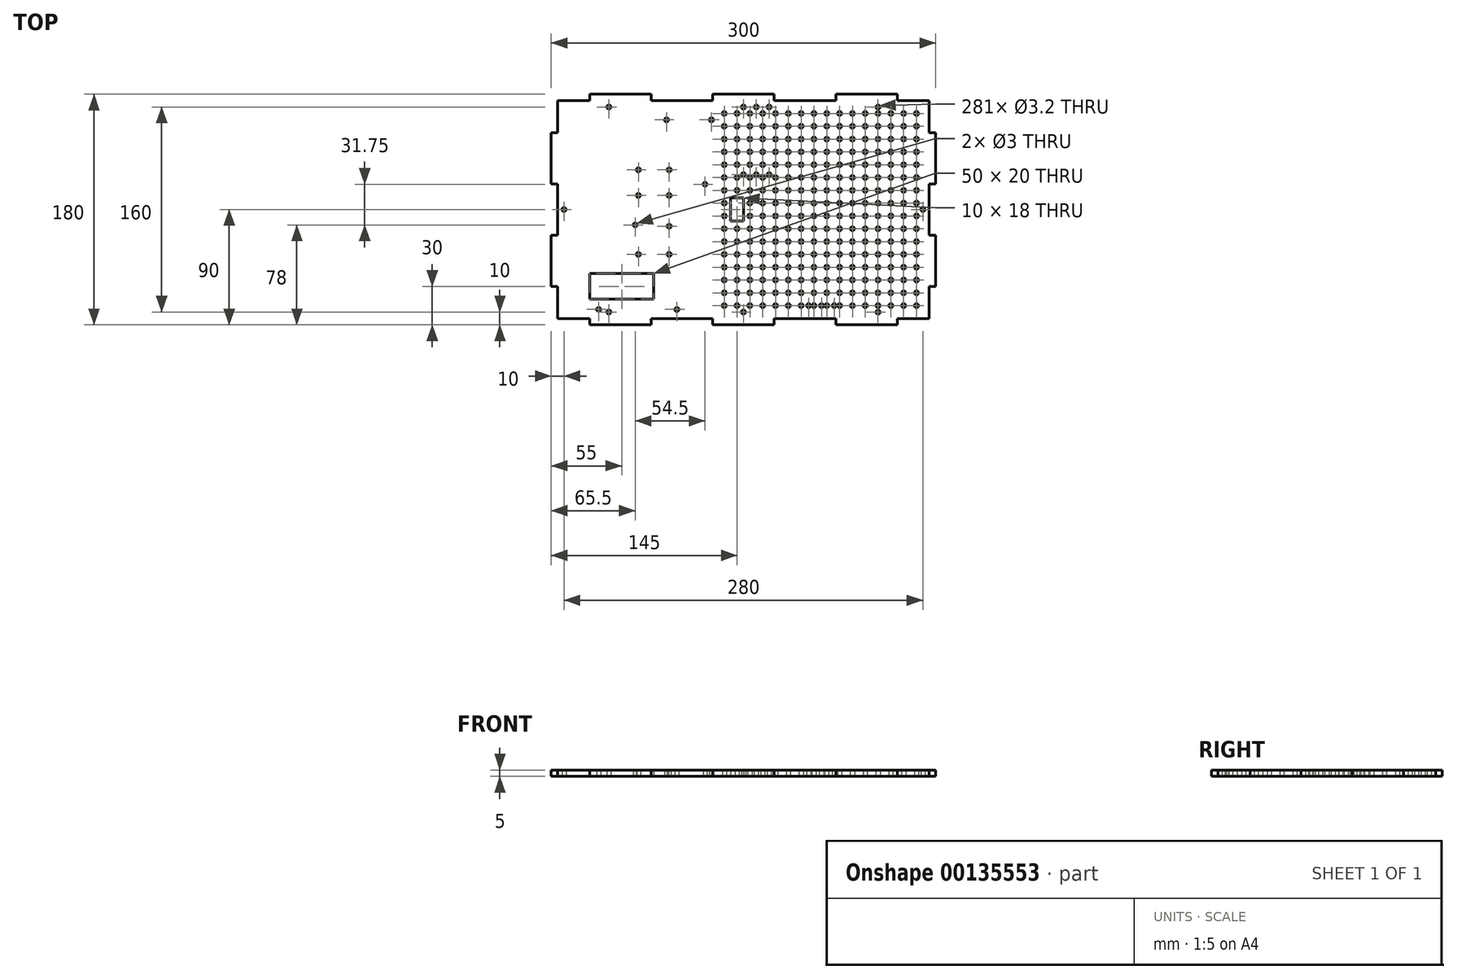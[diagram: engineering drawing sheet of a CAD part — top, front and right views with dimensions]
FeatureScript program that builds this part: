
annotation { "Feature Type Name" : "Feature", "Feature Type Description" : "" }
export const myFeature = defineFeature(function(context is Context, id is Id, definition is map)
    precondition{}
    {
        {
            var Q0;
            Q0=qCreatedBy(makeId("Top.planeOp"),FACE);
            var sketch = newSketch(context, id + "F0", { "sketchPlane" : qUnion([Q0])});
            skLineSegment(sketch, "E0", {"start": v(-150, 0) * mm, "end": v(150, 0) * mm, "construction": true});
            skLineSegment(sketch, "E1", {"start": v(0, 90) * mm, "end": v(0, -90) * mm, "construction": true});
            skLineSegment(sketch, "E2.bottom", {"start": v(-120, 90) * mm, "end": v(-72, 90) * mm});
            skLineSegment(sketch, "E2.top", {"start": v(-120, -90) * mm, "end": v(-72, -90) * mm});
            skLineSegment(sketch, "E2.left", {"start": v(-150, 60) * mm, "end": v(-150, -60) * mm});
            skLineSegment(sketch, "E2.right", {"start": v(150, 60) * mm, "end": v(150, -60) * mm});
            skLineSegment(sketch, "E3.bottom", {"start": v(-120, 85) * mm, "end": v(120, 85) * mm, "construction": true});
            skLineSegment(sketch, "E3.top", {"start": v(-145, -85) * mm, "end": v(145, -85) * mm, "construction": true});
            skLineSegment(sketch, "E3.left", {"start": v(-145, -60) * mm, "end": v(-145, -85) * mm, "construction": true});
            skLineSegment(sketch, "E3.right", {"start": v(145, -60) * mm, "end": v(145, -85) * mm, "construction": true});
            skLineSegment(sketch, "E4", {"start": v(-145, 85) * mm, "end": v(-120, 85) * mm});
            skLineSegment(sketch, "E5", {"start": v(-145, 85) * mm, "end": v(-145, 60) * mm});
            skLineSegment(sketch, "E6", {"start": v(-120, 85) * mm, "end": v(-120, 90) * mm});
            skLineSegment(sketch, "E7", {"start": v(-145, 60) * mm, "end": v(-150, 60) * mm});
            skLineSegment(sketch, "E8.MirrorCS", {"start": v(-120, -85) * mm, "end": v(-120, -90) * mm});
            skLineSegment(sketch, "E9.MirrorCS", {"start": v(-145, -85) * mm, "end": v(-120, -85) * mm});
            skLineSegment(sketch, "E10.MirrorCS", {"start": v(-145, -60) * mm, "end": v(-150, -60) * mm});
            skLineSegment(sketch, "E11.MirrorCS", {"start": v(-145, -85) * mm, "end": v(-145, -60) * mm});
            skLineSegment(sketch, "E12.MirrorCS", {"start": v(145, 60) * mm, "end": v(150, 60) * mm});
            skLineSegment(sketch, "E13.MirrorCS", {"start": v(145, 85) * mm, "end": v(145, 60) * mm});
            skLineSegment(sketch, "E14.MirrorCS", {"start": v(145, 85) * mm, "end": v(120, 85) * mm});
            skLineSegment(sketch, "E15.MirrorCS", {"start": v(120, 85) * mm, "end": v(120, 90) * mm});
            skLineSegment(sketch, "E16.MirrorCS", {"start": v(120, -85) * mm, "end": v(120, -90) * mm});
            skLineSegment(sketch, "E17.MirrorCS", {"start": v(145, -85) * mm, "end": v(120, -85) * mm});
            skLineSegment(sketch, "E18.MirrorCS", {"start": v(145, -85) * mm, "end": v(145, -60) * mm});
            skLineSegment(sketch, "E19.MirrorCS", {"start": v(145, -60) * mm, "end": v(150, -60) * mm});
            skLineSegment(sketch, "E20", {"start": v(-105, 112.7) * mm, "end": v(-105, -120.06) * mm, "construction": true});
            skLineSegment(sketch, "E21", {"start": v(105, 113.23) * mm, "end": v(105, -113.29) * mm, "construction": true});
            skLineSegment(sketch, "E22", {"start": v(-165.76, 80) * mm, "end": v(179.48, 80) * mm, "construction": true});
            skLineSegment(sketch, "E23", {"start": v(-160.04, -80) * mm, "end": v(189.9, -80) * mm, "construction": true});
            skLineSegment(sketch, "E24", {"start": v(140, 110.1) * mm, "end": v(140, -113.29) * mm, "construction": true});
            skLineSegment(sketch, "E25", {"start": v(-140, 116.87) * mm, "end": v(-140, -108.08) * mm, "construction": true});
            skCircle(sketch, "E26", {"center": v(0, 80) * mm, "radius": 1.6 * mm});
            skCircle(sketch, "E27", {"center": v(-105, 80) * mm, "radius": 1.6 * mm});
            skCircle(sketch, "E28", {"center": v(105, 80) * mm, "radius": 1.6 * mm});
            skCircle(sketch, "E29", {"center": v(140, 0) * mm, "radius": 1.6 * mm});
            skCircle(sketch, "E30", {"center": v(-140, 0) * mm, "radius": 1.6 * mm});
            skCircle(sketch, "E31", {"center": v(0, -80) * mm, "radius": 1.6 * mm});
            skCircle(sketch, "E32", {"center": v(105, -80) * mm, "radius": 1.6 * mm});
            skCircle(sketch, "E33", {"center": v(-105, -80) * mm, "radius": 1.6 * mm});
            skLineSegment(sketch, "E34", {"start": v(-72, 90) * mm, "end": v(-72, 85) * mm});
            skLineSegment(sketch, "E35.1.0.0", {"start": v(-72, 85) * mm, "end": v(-72, 90) * mm});
            skLineSegment(sketch, "E35.2.0.0", {"start": v(-24, 85) * mm, "end": v(-24, 90) * mm});
            skLineSegment(sketch, "E35.3.0.0", {"start": v(24, 85) * mm, "end": v(24, 90) * mm});
            skLineSegment(sketch, "E35.4.0.0", {"start": v(72, 85) * mm, "end": v(72, 90) * mm});
            skLineSegment(sketch, "E35.direction1", {"start": v(-120, 85) * mm, "end": v(-72, 85) * mm, "construction": true});
            skLineSegment(sketch, "E36", {"start": v(-72, 85) * mm, "end": v(-24, 85) * mm});
            skLineSegment(sketch, "E37", {"start": v(24, 85) * mm, "end": v(72, 85) * mm});
            skLineSegment(sketch, "E38.trimOffspring", {"start": v(72, 90) * mm, "end": v(120, 90) * mm});
            skLineSegment(sketch, "E39.trimOffspring", {"start": v(-24, 90) * mm, "end": v(24, 90) * mm});
            skLineSegment(sketch, "E40.MirrorCS", {"start": v(-24, -90) * mm, "end": v(24, -90) * mm});
            skLineSegment(sketch, "E41.MirrorCS", {"start": v(72, -90) * mm, "end": v(120, -90) * mm});
            skLineSegment(sketch, "E42.MirrorCS", {"start": v(24, -85) * mm, "end": v(24, -90) * mm});
            skLineSegment(sketch, "E43.MirrorCS", {"start": v(72, -85) * mm, "end": v(72, -90) * mm});
            skLineSegment(sketch, "E44.MirrorCS", {"start": v(-24, -85) * mm, "end": v(-24, -90) * mm});
            skLineSegment(sketch, "E45.MirrorCS", {"start": v(-72, -85) * mm, "end": v(-72, -90) * mm});
            skLineSegment(sketch, "E46", {"start": v(-72, -85) * mm, "end": v(-24, -85) * mm});
            skLineSegment(sketch, "E47", {"start": v(24, -85) * mm, "end": v(72, -85) * mm});
            skLineSegment(sketch, "E48", {"start": v(-145, 0) * mm, "end": v(-145, -20) * mm});
            skLineSegment(sketch, "E49", {"start": v(-145, -20) * mm, "end": v(-150, -20) * mm});
            skLineSegment(sketch, "E50", {"start": v(-144.23, 20) * mm, "end": v(-145, 20) * mm});
            skLineSegment(sketch, "E51", {"start": v(-145, 0) * mm, "end": v(-145, 20) * mm});
            skLineSegment(sketch, "E52.MirrorCS", {"start": v(145, -20) * mm, "end": v(150, -20) * mm});
            skLineSegment(sketch, "E53.MirrorCS", {"start": v(145, 0) * mm, "end": v(145, -20) * mm});
            skLineSegment(sketch, "E54.MirrorCS", {"start": v(145, 0) * mm, "end": v(145, 20) * mm});
            skLineSegment(sketch, "E55.MirrorCS", {"start": v(144.23, 20) * mm, "end": v(145, 20) * mm});
            skSolve(sketch);
        }
        {
            var Q0;
            Q0=qCreatedBy(makeId("Top.planeOp"),FACE);
            var sketch = newSketch(context, id + "F1", { "sketchPlane" : qUnion([Q0])});
            skLineSegment(sketch, "E56", {"start": v(-150, 0) * mm, "end": v(150, 0) * mm, "construction": true});
            skLineSegment(sketch, "E57", {"start": v(0, 90) * mm, "end": v(0, -90) * mm, "construction": true});
            skLineSegment(sketch, "E58.bottom", {"start": v(-120, 90) * mm, "end": v(-72, 90) * mm});
            skLineSegment(sketch, "E58.top", {"start": v(-120, -90) * mm, "end": v(-72, -90) * mm});
            skLineSegment(sketch, "E58.left", {"start": v(-150, 60) * mm, "end": v(-150, 20) * mm});
            skLineSegment(sketch, "E58.right", {"start": v(150, 60) * mm, "end": v(150, 20) * mm});
            skLineSegment(sketch, "E59.bottom", {"start": v(-120, 85) * mm, "end": v(120, 85) * mm, "construction": true});
            skLineSegment(sketch, "E59.top", {"start": v(-145, -85) * mm, "end": v(145, -85) * mm, "construction": true});
            skLineSegment(sketch, "E59.left", {"start": v(-145, -60) * mm, "end": v(-145, -85) * mm, "construction": true});
            skLineSegment(sketch, "E59.right", {"start": v(145, -60) * mm, "end": v(145, -85) * mm, "construction": true});
            skLineSegment(sketch, "E60", {"start": v(-145, 85) * mm, "end": v(-120, 85) * mm});
            skLineSegment(sketch, "E61", {"start": v(-145, 85) * mm, "end": v(-145, 60) * mm});
            skLineSegment(sketch, "E62", {"start": v(-120, 85) * mm, "end": v(-120, 90) * mm});
            skLineSegment(sketch, "E63", {"start": v(-145, 60) * mm, "end": v(-150, 60) * mm});
            skLineSegment(sketch, "E64.MirrorCS", {"start": v(-120, -85) * mm, "end": v(-120, -90) * mm});
            skLineSegment(sketch, "E65.MirrorCS", {"start": v(-145, -85) * mm, "end": v(-120, -85) * mm});
            skLineSegment(sketch, "E66.MirrorCS", {"start": v(-145, -60) * mm, "end": v(-150, -60) * mm});
            skLineSegment(sketch, "E67.MirrorCS", {"start": v(-145, -85) * mm, "end": v(-145, -60) * mm});
            skLineSegment(sketch, "E68.MirrorCS", {"start": v(145, 60) * mm, "end": v(150, 60) * mm});
            skLineSegment(sketch, "E69.MirrorCS", {"start": v(145, 85) * mm, "end": v(145, 60) * mm});
            skLineSegment(sketch, "E70.MirrorCS", {"start": v(145, 85) * mm, "end": v(120, 85) * mm});
            skLineSegment(sketch, "E71.MirrorCS", {"start": v(120, 85) * mm, "end": v(120, 90) * mm});
            skLineSegment(sketch, "E72.MirrorCS", {"start": v(120, -85) * mm, "end": v(120, -90) * mm});
            skLineSegment(sketch, "E73.MirrorCS", {"start": v(145, -85) * mm, "end": v(120, -85) * mm});
            skLineSegment(sketch, "E74.MirrorCS", {"start": v(145, -85) * mm, "end": v(145, -60) * mm});
            skLineSegment(sketch, "E75.MirrorCS", {"start": v(145, -60) * mm, "end": v(150, -60) * mm});
            skLineSegment(sketch, "E76", {"start": v(-105, 115.87) * mm, "end": v(-105, -116.9) * mm, "construction": true});
            skLineSegment(sketch, "E77", {"start": v(105, 116.39) * mm, "end": v(105, -110.13) * mm, "construction": true});
            skLineSegment(sketch, "E78", {"start": v(-165.91, 80) * mm, "end": v(179.33, 80) * mm, "construction": true});
            skLineSegment(sketch, "E79", {"start": v(-160.18, -80) * mm, "end": v(189.74, -80) * mm, "construction": true});
            skLineSegment(sketch, "E80", {"start": v(140, 113.26) * mm, "end": v(140, -110.13) * mm, "construction": true});
            skLineSegment(sketch, "E81", {"start": v(-140, 120.03) * mm, "end": v(-140, -104.92) * mm, "construction": true});
            skCircle(sketch, "E82", {"center": v(0, 80) * mm, "radius": 1.6 * mm});
            skCircle(sketch, "E83", {"center": v(-105, 80) * mm, "radius": 1.6 * mm});
            skCircle(sketch, "E84", {"center": v(105, 80) * mm, "radius": 1.6 * mm});
            skCircle(sketch, "E85", {"center": v(140, 0) * mm, "radius": 1.6 * mm});
            skCircle(sketch, "E86", {"center": v(-140, 0) * mm, "radius": 1.6 * mm});
            skCircle(sketch, "E87", {"center": v(0, -80) * mm, "radius": 1.6 * mm});
            skCircle(sketch, "E88", {"center": v(105, -80) * mm, "radius": 1.6 * mm});
            skCircle(sketch, "E89", {"center": v(-105, -80) * mm, "radius": 1.6 * mm});
            skLineSegment(sketch, "E90", {"start": v(-72, 90) * mm, "end": v(-72, 85) * mm});
            skLineSegment(sketch, "E91.1.0.0", {"start": v(-72, 85) * mm, "end": v(-72, 90) * mm});
            skLineSegment(sketch, "E91.2.0.0", {"start": v(-24, 85) * mm, "end": v(-24, 90) * mm});
            skLineSegment(sketch, "E91.3.0.0", {"start": v(24, 85) * mm, "end": v(24, 90) * mm});
            skLineSegment(sketch, "E91.4.0.0", {"start": v(72, 85) * mm, "end": v(72, 90) * mm});
            skLineSegment(sketch, "E91.direction1", {"start": v(-120, 85) * mm, "end": v(-72, 85) * mm, "construction": true});
            skLineSegment(sketch, "E92", {"start": v(-72, 85) * mm, "end": v(-24, 85) * mm});
            skLineSegment(sketch, "E93", {"start": v(24, 85) * mm, "end": v(72, 85) * mm});
            skLineSegment(sketch, "E94.trimOffspring", {"start": v(72, 90) * mm, "end": v(120, 90) * mm});
            skLineSegment(sketch, "E95.trimOffspring", {"start": v(-24, 90) * mm, "end": v(24, 90) * mm});
            skLineSegment(sketch, "E96.MirrorCS", {"start": v(-24, -90) * mm, "end": v(24, -90) * mm});
            skLineSegment(sketch, "E97.MirrorCS", {"start": v(72, -90) * mm, "end": v(120, -90) * mm});
            skLineSegment(sketch, "E98.MirrorCS", {"start": v(24, -85) * mm, "end": v(24, -90) * mm});
            skLineSegment(sketch, "E99.MirrorCS", {"start": v(72, -85) * mm, "end": v(72, -90) * mm});
            skLineSegment(sketch, "E100.MirrorCS", {"start": v(-24, -85) * mm, "end": v(-24, -90) * mm});
            skLineSegment(sketch, "E101.MirrorCS", {"start": v(-72, -85) * mm, "end": v(-72, -90) * mm});
            skLineSegment(sketch, "E102", {"start": v(-72, -85) * mm, "end": v(-24, -85) * mm});
            skLineSegment(sketch, "E103", {"start": v(24, -85) * mm, "end": v(72, -85) * mm});
            skLineSegment(sketch, "E104", {"start": v(-145, 0) * mm, "end": v(-145, -20) * mm});
            skLineSegment(sketch, "E105", {"start": v(-145, -20) * mm, "end": v(-150, -20) * mm});
            skLineSegment(sketch, "E106", {"start": v(-145, 0) * mm, "end": v(-145, 20) * mm});
            skLineSegment(sketch, "E107.MirrorCS", {"start": v(145, -20) * mm, "end": v(150, -20) * mm});
            skLineSegment(sketch, "E108.MirrorCS", {"start": v(145, 0) * mm, "end": v(145, -20) * mm});
            skLineSegment(sketch, "E109.MirrorCS", {"start": v(145, 0) * mm, "end": v(145, 20) * mm});
            skLineSegment(sketch, "E110", {"start": v(-145, 20) * mm, "end": v(-150, 20) * mm});
            skLineSegment(sketch, "E111", {"start": v(145, 20) * mm, "end": v(150, 20) * mm});
            skLineSegment(sketch, "E112.trimOffspring", {"start": v(-150, -20) * mm, "end": v(-150, -60) * mm});
            skLineSegment(sketch, "E113.trimOffspring", {"start": v(150, -20) * mm, "end": v(150, -60) * mm});
            skLineSegment(sketch, "E114.bottom", {"start": v(-15, 75) * mm, "end": v(135, 75) * mm, "construction": true});
            skLineSegment(sketch, "E114.top", {"start": v(-15, -75) * mm, "end": v(135, -75) * mm, "construction": true});
            skLineSegment(sketch, "E114.left", {"start": v(-15, 75) * mm, "end": v(-15, -75) * mm, "construction": true});
            skLineSegment(sketch, "E114.right", {"start": v(135, 75) * mm, "end": v(135, -75) * mm, "construction": true});
            skCircle(sketch, "E115", {"center": v(135, -75) * mm, "radius": 1.6 * mm});
            skCircle(sketch, "E116.0.1.0", {"center": v(135, -65) * mm, "radius": 1.6 * mm});
            skCircle(sketch, "E116.0.2.0", {"center": v(135, -55) * mm, "radius": 1.6 * mm});
            skCircle(sketch, "E116.0.3.0", {"center": v(135, -45) * mm, "radius": 1.6 * mm});
            skCircle(sketch, "E116.0.4.0", {"center": v(135, -35) * mm, "radius": 1.6 * mm});
            skCircle(sketch, "E116.0.5.0", {"center": v(135, -25) * mm, "radius": 1.6 * mm});
            skCircle(sketch, "E116.0.6.0", {"center": v(135, -15) * mm, "radius": 1.6 * mm});
            skCircle(sketch, "E116.0.7.0", {"center": v(135, -5) * mm, "radius": 1.6 * mm});
            skCircle(sketch, "E116.0.8.0", {"center": v(135, 5) * mm, "radius": 1.6 * mm});
            skCircle(sketch, "E116.0.9.0", {"center": v(135, 15) * mm, "radius": 1.6 * mm});
            skCircle(sketch, "E116.0.10.0", {"center": v(135, 25) * mm, "radius": 1.6 * mm});
            skCircle(sketch, "E116.0.11.0", {"center": v(135, 35) * mm, "radius": 1.6 * mm});
            skCircle(sketch, "E116.0.12.0", {"center": v(135, 45) * mm, "radius": 1.6 * mm});
            skCircle(sketch, "E116.0.13.0", {"center": v(135, 55) * mm, "radius": 1.6 * mm});
            skCircle(sketch, "E116.0.14.0", {"center": v(135, 65) * mm, "radius": 1.6 * mm});
            skCircle(sketch, "E116.1.0.0", {"center": v(125, -75) * mm, "radius": 1.6 * mm});
            skCircle(sketch, "E116.1.1.0", {"center": v(125, -65) * mm, "radius": 1.6 * mm});
            skCircle(sketch, "E116.1.2.0", {"center": v(125, -55) * mm, "radius": 1.6 * mm});
            skCircle(sketch, "E116.1.3.0", {"center": v(125, -45) * mm, "radius": 1.6 * mm});
            skCircle(sketch, "E116.1.4.0", {"center": v(125, -35) * mm, "radius": 1.6 * mm});
            skCircle(sketch, "E116.1.5.0", {"center": v(125, -25) * mm, "radius": 1.6 * mm});
            skCircle(sketch, "E116.1.6.0", {"center": v(125, -15) * mm, "radius": 1.6 * mm});
            skCircle(sketch, "E116.1.7.0", {"center": v(125, -5) * mm, "radius": 1.6 * mm});
            skCircle(sketch, "E116.1.8.0", {"center": v(125, 5) * mm, "radius": 1.6 * mm});
            skCircle(sketch, "E116.1.9.0", {"center": v(125, 15) * mm, "radius": 1.6 * mm});
            skCircle(sketch, "E116.1.10.0", {"center": v(125, 25) * mm, "radius": 1.6 * mm});
            skCircle(sketch, "E116.1.11.0", {"center": v(125, 35) * mm, "radius": 1.6 * mm});
            skCircle(sketch, "E116.1.12.0", {"center": v(125, 45) * mm, "radius": 1.6 * mm});
            skCircle(sketch, "E116.1.13.0", {"center": v(125, 55) * mm, "radius": 1.6 * mm});
            skCircle(sketch, "E116.1.14.0", {"center": v(125, 65) * mm, "radius": 1.6 * mm});
            skCircle(sketch, "E116.2.0.0", {"center": v(115, -75) * mm, "radius": 1.6 * mm});
            skCircle(sketch, "E116.2.1.0", {"center": v(115, -65) * mm, "radius": 1.6 * mm});
            skCircle(sketch, "E116.2.2.0", {"center": v(115, -55) * mm, "radius": 1.6 * mm});
            skCircle(sketch, "E116.2.3.0", {"center": v(115, -45) * mm, "radius": 1.6 * mm});
            skCircle(sketch, "E116.2.4.0", {"center": v(115, -35) * mm, "radius": 1.6 * mm});
            skCircle(sketch, "E116.2.5.0", {"center": v(115, -25) * mm, "radius": 1.6 * mm});
            skCircle(sketch, "E116.2.6.0", {"center": v(115, -15) * mm, "radius": 1.6 * mm});
            skCircle(sketch, "E116.2.7.0", {"center": v(115, -5) * mm, "radius": 1.6 * mm});
            skCircle(sketch, "E116.2.8.0", {"center": v(115, 5) * mm, "radius": 1.6 * mm});
            skCircle(sketch, "E116.2.9.0", {"center": v(115, 15) * mm, "radius": 1.6 * mm});
            skCircle(sketch, "E116.2.10.0", {"center": v(115, 25) * mm, "radius": 1.6 * mm});
            skCircle(sketch, "E116.2.11.0", {"center": v(115, 35) * mm, "radius": 1.6 * mm});
            skCircle(sketch, "E116.2.12.0", {"center": v(115, 45) * mm, "radius": 1.6 * mm});
            skCircle(sketch, "E116.2.13.0", {"center": v(115, 55) * mm, "radius": 1.6 * mm});
            skCircle(sketch, "E116.2.14.0", {"center": v(115, 65) * mm, "radius": 1.6 * mm});
            skCircle(sketch, "E116.3.0.0", {"center": v(105, -75) * mm, "radius": 1.6 * mm});
            skCircle(sketch, "E116.3.1.0", {"center": v(105, -65) * mm, "radius": 1.6 * mm});
            skCircle(sketch, "E116.3.2.0", {"center": v(105, -55) * mm, "radius": 1.6 * mm});
            skCircle(sketch, "E116.3.3.0", {"center": v(105, -45) * mm, "radius": 1.6 * mm});
            skCircle(sketch, "E116.3.4.0", {"center": v(105, -35) * mm, "radius": 1.6 * mm});
            skCircle(sketch, "E116.3.5.0", {"center": v(105, -25) * mm, "radius": 1.6 * mm});
            skCircle(sketch, "E116.3.6.0", {"center": v(105, -15) * mm, "radius": 1.6 * mm});
            skCircle(sketch, "E116.3.7.0", {"center": v(105, -5) * mm, "radius": 1.6 * mm});
            skCircle(sketch, "E116.3.8.0", {"center": v(105, 5) * mm, "radius": 1.6 * mm});
            skCircle(sketch, "E116.3.9.0", {"center": v(105, 15) * mm, "radius": 1.6 * mm});
            skCircle(sketch, "E116.3.10.0", {"center": v(105, 25) * mm, "radius": 1.6 * mm});
            skCircle(sketch, "E116.3.11.0", {"center": v(105, 35) * mm, "radius": 1.6 * mm});
            skCircle(sketch, "E116.3.12.0", {"center": v(105, 45) * mm, "radius": 1.6 * mm});
            skCircle(sketch, "E116.3.13.0", {"center": v(105, 55) * mm, "radius": 1.6 * mm});
            skCircle(sketch, "E116.3.14.0", {"center": v(105, 65) * mm, "radius": 1.6 * mm});
            skCircle(sketch, "E116.4.0.0", {"center": v(95, -75) * mm, "radius": 1.6 * mm});
            skCircle(sketch, "E116.4.1.0", {"center": v(95, -65) * mm, "radius": 1.6 * mm});
            skCircle(sketch, "E116.4.2.0", {"center": v(95, -55) * mm, "radius": 1.6 * mm});
            skCircle(sketch, "E116.4.3.0", {"center": v(95, -45) * mm, "radius": 1.6 * mm});
            skCircle(sketch, "E116.4.4.0", {"center": v(95, -35) * mm, "radius": 1.6 * mm});
            skCircle(sketch, "E116.4.5.0", {"center": v(95, -25) * mm, "radius": 1.6 * mm});
            skCircle(sketch, "E116.4.6.0", {"center": v(95, -15) * mm, "radius": 1.6 * mm});
            skCircle(sketch, "E116.4.7.0", {"center": v(95, -5) * mm, "radius": 1.6 * mm});
            skCircle(sketch, "E116.4.8.0", {"center": v(95, 5) * mm, "radius": 1.6 * mm});
            skCircle(sketch, "E116.4.9.0", {"center": v(95, 15) * mm, "radius": 1.6 * mm});
            skCircle(sketch, "E116.4.10.0", {"center": v(95, 25) * mm, "radius": 1.6 * mm});
            skCircle(sketch, "E116.4.11.0", {"center": v(95, 35) * mm, "radius": 1.6 * mm});
            skCircle(sketch, "E116.4.12.0", {"center": v(95, 45) * mm, "radius": 1.6 * mm});
            skCircle(sketch, "E116.4.13.0", {"center": v(95, 55) * mm, "radius": 1.6 * mm});
            skCircle(sketch, "E116.4.14.0", {"center": v(95, 65) * mm, "radius": 1.6 * mm});
            skCircle(sketch, "E116.5.0.0", {"center": v(85, -75) * mm, "radius": 1.6 * mm});
            skCircle(sketch, "E116.5.1.0", {"center": v(85, -65) * mm, "radius": 1.6 * mm});
            skCircle(sketch, "E116.5.2.0", {"center": v(85, -55) * mm, "radius": 1.6 * mm});
            skCircle(sketch, "E116.5.3.0", {"center": v(85, -45) * mm, "radius": 1.6 * mm});
            skCircle(sketch, "E116.5.4.0", {"center": v(85, -35) * mm, "radius": 1.6 * mm});
            skCircle(sketch, "E116.5.5.0", {"center": v(85, -25) * mm, "radius": 1.6 * mm});
            skCircle(sketch, "E116.5.6.0", {"center": v(85, -15) * mm, "radius": 1.6 * mm});
            skCircle(sketch, "E116.5.7.0", {"center": v(85, -5) * mm, "radius": 1.6 * mm});
            skCircle(sketch, "E116.5.8.0", {"center": v(85, 5) * mm, "radius": 1.6 * mm});
            skCircle(sketch, "E116.5.9.0", {"center": v(85, 15) * mm, "radius": 1.6 * mm});
            skCircle(sketch, "E116.5.10.0", {"center": v(85, 25) * mm, "radius": 1.6 * mm});
            skCircle(sketch, "E116.5.11.0", {"center": v(85, 35) * mm, "radius": 1.6 * mm});
            skCircle(sketch, "E116.5.12.0", {"center": v(85, 45) * mm, "radius": 1.6 * mm});
            skCircle(sketch, "E116.5.13.0", {"center": v(85, 55) * mm, "radius": 1.6 * mm});
            skCircle(sketch, "E116.5.14.0", {"center": v(85, 65) * mm, "radius": 1.6 * mm});
            skCircle(sketch, "E116.6.0.0", {"center": v(75, -75) * mm, "radius": 1.6 * mm});
            skCircle(sketch, "E116.6.1.0", {"center": v(75, -65) * mm, "radius": 1.6 * mm});
            skCircle(sketch, "E116.6.2.0", {"center": v(75, -55) * mm, "radius": 1.6 * mm});
            skCircle(sketch, "E116.6.3.0", {"center": v(75, -45) * mm, "radius": 1.6 * mm});
            skCircle(sketch, "E116.6.4.0", {"center": v(75, -35) * mm, "radius": 1.6 * mm});
            skCircle(sketch, "E116.6.5.0", {"center": v(75, -25) * mm, "radius": 1.6 * mm});
            skCircle(sketch, "E116.6.6.0", {"center": v(75, -15) * mm, "radius": 1.6 * mm});
            skCircle(sketch, "E116.6.7.0", {"center": v(75, -5) * mm, "radius": 1.6 * mm});
            skCircle(sketch, "E116.6.8.0", {"center": v(75, 5) * mm, "radius": 1.6 * mm});
            skCircle(sketch, "E116.6.9.0", {"center": v(75, 15) * mm, "radius": 1.6 * mm});
            skCircle(sketch, "E116.6.10.0", {"center": v(75, 25) * mm, "radius": 1.6 * mm});
            skCircle(sketch, "E116.6.11.0", {"center": v(75, 35) * mm, "radius": 1.6 * mm});
            skCircle(sketch, "E116.6.12.0", {"center": v(75, 45) * mm, "radius": 1.6 * mm});
            skCircle(sketch, "E116.6.13.0", {"center": v(75, 55) * mm, "radius": 1.6 * mm});
            skCircle(sketch, "E116.6.14.0", {"center": v(75, 65) * mm, "radius": 1.6 * mm});
            skCircle(sketch, "E116.7.0.0", {"center": v(65, -75) * mm, "radius": 1.6 * mm});
            skCircle(sketch, "E116.7.1.0", {"center": v(65, -65) * mm, "radius": 1.6 * mm});
            skCircle(sketch, "E116.7.2.0", {"center": v(65, -55) * mm, "radius": 1.6 * mm});
            skCircle(sketch, "E116.7.3.0", {"center": v(65, -45) * mm, "radius": 1.6 * mm});
            skCircle(sketch, "E116.7.4.0", {"center": v(65, -35) * mm, "radius": 1.6 * mm});
            skCircle(sketch, "E116.7.5.0", {"center": v(65, -25) * mm, "radius": 1.6 * mm});
            skCircle(sketch, "E116.7.6.0", {"center": v(65, -15) * mm, "radius": 1.6 * mm});
            skCircle(sketch, "E116.7.7.0", {"center": v(65, -5) * mm, "radius": 1.6 * mm});
            skCircle(sketch, "E116.7.8.0", {"center": v(65, 5) * mm, "radius": 1.6 * mm});
            skCircle(sketch, "E116.7.9.0", {"center": v(65, 15) * mm, "radius": 1.6 * mm});
            skCircle(sketch, "E116.7.10.0", {"center": v(65, 25) * mm, "radius": 1.6 * mm});
            skCircle(sketch, "E116.7.11.0", {"center": v(65, 35) * mm, "radius": 1.6 * mm});
            skCircle(sketch, "E116.7.12.0", {"center": v(65, 45) * mm, "radius": 1.6 * mm});
            skCircle(sketch, "E116.7.13.0", {"center": v(65, 55) * mm, "radius": 1.6 * mm});
            skCircle(sketch, "E116.7.14.0", {"center": v(65, 65) * mm, "radius": 1.6 * mm});
            skCircle(sketch, "E116.8.0.0", {"center": v(55, -75) * mm, "radius": 1.6 * mm});
            skCircle(sketch, "E116.8.1.0", {"center": v(55, -65) * mm, "radius": 1.6 * mm});
            skCircle(sketch, "E116.8.2.0", {"center": v(55, -55) * mm, "radius": 1.6 * mm});
            skCircle(sketch, "E116.8.3.0", {"center": v(55, -45) * mm, "radius": 1.6 * mm});
            skCircle(sketch, "E116.8.4.0", {"center": v(55, -35) * mm, "radius": 1.6 * mm});
            skCircle(sketch, "E116.8.5.0", {"center": v(55, -25) * mm, "radius": 1.6 * mm});
            skCircle(sketch, "E116.8.6.0", {"center": v(55, -15) * mm, "radius": 1.6 * mm});
            skCircle(sketch, "E116.8.7.0", {"center": v(55, -5) * mm, "radius": 1.6 * mm});
            skCircle(sketch, "E116.8.8.0", {"center": v(55, 5) * mm, "radius": 1.6 * mm});
            skCircle(sketch, "E116.8.9.0", {"center": v(55, 15) * mm, "radius": 1.6 * mm});
            skCircle(sketch, "E116.8.10.0", {"center": v(55, 25) * mm, "radius": 1.6 * mm});
            skCircle(sketch, "E116.8.11.0", {"center": v(55, 35) * mm, "radius": 1.6 * mm});
            skCircle(sketch, "E116.8.12.0", {"center": v(55, 45) * mm, "radius": 1.6 * mm});
            skCircle(sketch, "E116.8.13.0", {"center": v(55, 55) * mm, "radius": 1.6 * mm});
            skCircle(sketch, "E116.8.14.0", {"center": v(55, 65) * mm, "radius": 1.6 * mm});
            skCircle(sketch, "E116.9.0.0", {"center": v(45, -75) * mm, "radius": 1.6 * mm});
            skCircle(sketch, "E116.9.1.0", {"center": v(45, -65) * mm, "radius": 1.6 * mm});
            skCircle(sketch, "E116.9.2.0", {"center": v(45, -55) * mm, "radius": 1.6 * mm});
            skCircle(sketch, "E116.9.3.0", {"center": v(45, -45) * mm, "radius": 1.6 * mm});
            skCircle(sketch, "E116.9.4.0", {"center": v(45, -35) * mm, "radius": 1.6 * mm});
            skCircle(sketch, "E116.9.5.0", {"center": v(45, -25) * mm, "radius": 1.6 * mm});
            skCircle(sketch, "E116.9.6.0", {"center": v(45, -15) * mm, "radius": 1.6 * mm});
            skCircle(sketch, "E116.9.7.0", {"center": v(45, -5) * mm, "radius": 1.6 * mm});
            skCircle(sketch, "E116.9.8.0", {"center": v(45, 5) * mm, "radius": 1.6 * mm});
            skCircle(sketch, "E116.9.9.0", {"center": v(45, 15) * mm, "radius": 1.6 * mm});
            skCircle(sketch, "E116.9.10.0", {"center": v(45, 25) * mm, "radius": 1.6 * mm});
            skCircle(sketch, "E116.9.11.0", {"center": v(45, 35) * mm, "radius": 1.6 * mm});
            skCircle(sketch, "E116.9.12.0", {"center": v(45, 45) * mm, "radius": 1.6 * mm});
            skCircle(sketch, "E116.9.13.0", {"center": v(45, 55) * mm, "radius": 1.6 * mm});
            skCircle(sketch, "E116.9.14.0", {"center": v(45, 65) * mm, "radius": 1.6 * mm});
            skCircle(sketch, "E116.10.0.0", {"center": v(35, -75) * mm, "radius": 1.6 * mm});
            skCircle(sketch, "E116.10.1.0", {"center": v(35, -65) * mm, "radius": 1.6 * mm});
            skCircle(sketch, "E116.10.2.0", {"center": v(35, -55) * mm, "radius": 1.6 * mm});
            skCircle(sketch, "E116.10.3.0", {"center": v(35, -45) * mm, "radius": 1.6 * mm});
            skCircle(sketch, "E116.10.4.0", {"center": v(35, -35) * mm, "radius": 1.6 * mm});
            skCircle(sketch, "E116.10.5.0", {"center": v(35, -25) * mm, "radius": 1.6 * mm});
            skCircle(sketch, "E116.10.6.0", {"center": v(35, -15) * mm, "radius": 1.6 * mm});
            skCircle(sketch, "E116.10.7.0", {"center": v(35, -5) * mm, "radius": 1.6 * mm});
            skCircle(sketch, "E116.10.8.0", {"center": v(35, 5) * mm, "radius": 1.6 * mm});
            skCircle(sketch, "E116.10.9.0", {"center": v(35, 15) * mm, "radius": 1.6 * mm});
            skCircle(sketch, "E116.10.10.0", {"center": v(35, 25) * mm, "radius": 1.6 * mm});
            skCircle(sketch, "E116.10.11.0", {"center": v(35, 35) * mm, "radius": 1.6 * mm});
            skCircle(sketch, "E116.10.12.0", {"center": v(35, 45) * mm, "radius": 1.6 * mm});
            skCircle(sketch, "E116.10.13.0", {"center": v(35, 55) * mm, "radius": 1.6 * mm});
            skCircle(sketch, "E116.10.14.0", {"center": v(35, 65) * mm, "radius": 1.6 * mm});
            skCircle(sketch, "E116.11.0.0", {"center": v(25, -75) * mm, "radius": 1.6 * mm});
            skCircle(sketch, "E116.11.1.0", {"center": v(25, -65) * mm, "radius": 1.6 * mm});
            skCircle(sketch, "E116.11.2.0", {"center": v(25, -55) * mm, "radius": 1.6 * mm});
            skCircle(sketch, "E116.11.3.0", {"center": v(25, -45) * mm, "radius": 1.6 * mm});
            skCircle(sketch, "E116.11.4.0", {"center": v(25, -35) * mm, "radius": 1.6 * mm});
            skCircle(sketch, "E116.11.5.0", {"center": v(25, -25) * mm, "radius": 1.6 * mm});
            skCircle(sketch, "E116.11.6.0", {"center": v(25, -15) * mm, "radius": 1.6 * mm});
            skCircle(sketch, "E116.11.7.0", {"center": v(25, -5) * mm, "radius": 1.6 * mm});
            skCircle(sketch, "E116.11.8.0", {"center": v(25, 5) * mm, "radius": 1.6 * mm});
            skCircle(sketch, "E116.11.9.0", {"center": v(25, 15) * mm, "radius": 1.6 * mm});
            skCircle(sketch, "E116.11.10.0", {"center": v(25, 25) * mm, "radius": 1.6 * mm});
            skCircle(sketch, "E116.11.11.0", {"center": v(25, 35) * mm, "radius": 1.6 * mm});
            skCircle(sketch, "E116.11.12.0", {"center": v(25, 45) * mm, "radius": 1.6 * mm});
            skCircle(sketch, "E116.11.13.0", {"center": v(25, 55) * mm, "radius": 1.6 * mm});
            skCircle(sketch, "E116.11.14.0", {"center": v(25, 65) * mm, "radius": 1.6 * mm});
            skCircle(sketch, "E116.12.0.0", {"center": v(15, -75) * mm, "radius": 1.6 * mm});
            skCircle(sketch, "E116.12.1.0", {"center": v(15, -65) * mm, "radius": 1.6 * mm});
            skCircle(sketch, "E116.12.2.0", {"center": v(15, -55) * mm, "radius": 1.6 * mm});
            skCircle(sketch, "E116.12.3.0", {"center": v(15, -45) * mm, "radius": 1.6 * mm});
            skCircle(sketch, "E116.12.4.0", {"center": v(15, -35) * mm, "radius": 1.6 * mm});
            skCircle(sketch, "E116.12.5.0", {"center": v(15, -25) * mm, "radius": 1.6 * mm});
            skCircle(sketch, "E116.12.6.0", {"center": v(15, -15) * mm, "radius": 1.6 * mm});
            skCircle(sketch, "E116.12.7.0", {"center": v(15, -5) * mm, "radius": 1.6 * mm});
            skCircle(sketch, "E116.12.8.0", {"center": v(15, 5) * mm, "radius": 1.6 * mm});
            skCircle(sketch, "E116.12.9.0", {"center": v(15, 15) * mm, "radius": 1.6 * mm});
            skCircle(sketch, "E116.12.10.0", {"center": v(15, 25) * mm, "radius": 1.6 * mm});
            skCircle(sketch, "E116.12.11.0", {"center": v(15, 35) * mm, "radius": 1.6 * mm});
            skCircle(sketch, "E116.12.12.0", {"center": v(15, 45) * mm, "radius": 1.6 * mm});
            skCircle(sketch, "E116.12.13.0", {"center": v(15, 55) * mm, "radius": 1.6 * mm});
            skCircle(sketch, "E116.12.14.0", {"center": v(15, 65) * mm, "radius": 1.6 * mm});
            skLineSegment(sketch, "E116.direction1", {"start": v(135, -75) * mm, "end": v(125, -75) * mm, "construction": true});
            skLineSegment(sketch, "E116.direction2", {"start": v(135, -75) * mm, "end": v(135, -65) * mm, "construction": true});
            skCircle(sketch, "E117.0.0.15", {"center": v(135, 75) * mm, "radius": 1.6 * mm});
            skCircle(sketch, "E117.0.1.15", {"center": v(125, 75) * mm, "radius": 1.6 * mm});
            skCircle(sketch, "E117.0.2.15", {"center": v(115, 75) * mm, "radius": 1.6 * mm});
            skCircle(sketch, "E117.0.3.15", {"center": v(105, 75) * mm, "radius": 1.6 * mm});
            skCircle(sketch, "E117.0.4.15", {"center": v(95, 75) * mm, "radius": 1.6 * mm});
            skCircle(sketch, "E117.0.5.15", {"center": v(85, 75) * mm, "radius": 1.6 * mm});
            skCircle(sketch, "E117.0.6.15", {"center": v(75, 75) * mm, "radius": 1.6 * mm});
            skCircle(sketch, "E117.0.7.15", {"center": v(65, 75) * mm, "radius": 1.6 * mm});
            skCircle(sketch, "E117.0.8.15", {"center": v(55, 75) * mm, "radius": 1.6 * mm});
            skCircle(sketch, "E117.0.9.15", {"center": v(45, 75) * mm, "radius": 1.6 * mm});
            skCircle(sketch, "E117.0.10.15", {"center": v(35, 75) * mm, "radius": 1.6 * mm});
            skCircle(sketch, "E117.0.11.15", {"center": v(25, 75) * mm, "radius": 1.6 * mm});
            skCircle(sketch, "E117.0.12.15", {"center": v(15, 75) * mm, "radius": 1.6 * mm});
            skCircle(sketch, "E118.0.13.0", {"center": v(5, -75) * mm, "radius": 1.6 * mm});
            skCircle(sketch, "E118.0.13.1", {"center": v(5, -65) * mm, "radius": 1.6 * mm});
            skCircle(sketch, "E118.0.13.2", {"center": v(5, -55) * mm, "radius": 1.6 * mm});
            skCircle(sketch, "E118.0.13.3", {"center": v(5, -45) * mm, "radius": 1.6 * mm});
            skCircle(sketch, "E118.0.13.4", {"center": v(5, -35) * mm, "radius": 1.6 * mm});
            skCircle(sketch, "E118.0.13.5", {"center": v(5, -25) * mm, "radius": 1.6 * mm});
            skCircle(sketch, "E118.0.13.6", {"center": v(5, -15) * mm, "radius": 1.6 * mm});
            skCircle(sketch, "E118.0.13.7", {"center": v(5, -5) * mm, "radius": 1.6 * mm});
            skCircle(sketch, "E118.0.13.8", {"center": v(5, 5) * mm, "radius": 1.6 * mm});
            skCircle(sketch, "E118.0.13.9", {"center": v(5, 15) * mm, "radius": 1.6 * mm});
            skCircle(sketch, "E118.0.13.10", {"center": v(5, 25) * mm, "radius": 1.6 * mm});
            skCircle(sketch, "E118.0.13.11", {"center": v(5, 35) * mm, "radius": 1.6 * mm});
            skCircle(sketch, "E118.0.13.12", {"center": v(5, 45) * mm, "radius": 1.6 * mm});
            skCircle(sketch, "E118.0.13.13", {"center": v(5, 55) * mm, "radius": 1.6 * mm});
            skCircle(sketch, "E118.0.13.14", {"center": v(5, 65) * mm, "radius": 1.6 * mm});
            skCircle(sketch, "E118.0.13.15", {"center": v(5, 75) * mm, "radius": 1.6 * mm});
            skCircle(sketch, "E118.0.14.0", {"center": v(-5, -75) * mm, "radius": 1.6 * mm});
            skCircle(sketch, "E118.0.14.1", {"center": v(-5, -65) * mm, "radius": 1.6 * mm});
            skCircle(sketch, "E118.0.14.2", {"center": v(-5, -55) * mm, "radius": 1.6 * mm});
            skCircle(sketch, "E118.0.14.3", {"center": v(-5, -45) * mm, "radius": 1.6 * mm});
            skCircle(sketch, "E118.0.14.4", {"center": v(-5, -35) * mm, "radius": 1.6 * mm});
            skCircle(sketch, "E118.0.14.5", {"center": v(-5, -25) * mm, "radius": 1.6 * mm});
            skCircle(sketch, "E118.0.14.6", {"center": v(-5, -15) * mm, "radius": 1.6 * mm});
            skCircle(sketch, "E118.0.14.9", {"center": v(-5, 15) * mm, "radius": 1.6 * mm});
            skCircle(sketch, "E118.0.14.10", {"center": v(-5, 25) * mm, "radius": 1.6 * mm});
            skCircle(sketch, "E118.0.14.11", {"center": v(-5, 35) * mm, "radius": 1.6 * mm});
            skCircle(sketch, "E118.0.14.12", {"center": v(-5, 45) * mm, "radius": 1.6 * mm});
            skCircle(sketch, "E118.0.14.13", {"center": v(-5, 55) * mm, "radius": 1.6 * mm});
            skCircle(sketch, "E118.0.14.14", {"center": v(-5, 65) * mm, "radius": 1.6 * mm});
            skCircle(sketch, "E118.0.14.15", {"center": v(-5, 75) * mm, "radius": 1.6 * mm});
            skCircle(sketch, "E118.0.15.0", {"center": v(-15, -75) * mm, "radius": 1.6 * mm});
            skCircle(sketch, "E118.0.15.1", {"center": v(-15, -65) * mm, "radius": 1.6 * mm});
            skCircle(sketch, "E118.0.15.2", {"center": v(-15, -55) * mm, "radius": 1.6 * mm});
            skCircle(sketch, "E118.0.15.3", {"center": v(-15, -45) * mm, "radius": 1.6 * mm});
            skCircle(sketch, "E118.0.15.4", {"center": v(-15, -35) * mm, "radius": 1.6 * mm});
            skCircle(sketch, "E118.0.15.5", {"center": v(-15, -25) * mm, "radius": 1.6 * mm});
            skCircle(sketch, "E118.0.15.6", {"center": v(-15, -15) * mm, "radius": 1.6 * mm});
            skCircle(sketch, "E118.0.15.7", {"center": v(-15, -5) * mm, "radius": 1.6 * mm});
            skCircle(sketch, "E118.0.15.8", {"center": v(-15, 5) * mm, "radius": 1.6 * mm});
            skCircle(sketch, "E118.0.15.9", {"center": v(-15, 15) * mm, "radius": 1.6 * mm});
            skCircle(sketch, "E118.0.15.10", {"center": v(-15, 25) * mm, "radius": 1.6 * mm});
            skCircle(sketch, "E118.0.15.11", {"center": v(-15, 35) * mm, "radius": 1.6 * mm});
            skCircle(sketch, "E118.0.15.12", {"center": v(-15, 45) * mm, "radius": 1.6 * mm});
            skCircle(sketch, "E118.0.15.13", {"center": v(-15, 55) * mm, "radius": 1.6 * mm});
            skCircle(sketch, "E118.0.15.14", {"center": v(-15, 65) * mm, "radius": 1.6 * mm});
            skCircle(sketch, "E118.0.15.15", {"center": v(-15, 75) * mm, "radius": 1.6 * mm});
            skLineSegment(sketch, "E119", {"start": v(-126.3, -60) * mm, "end": v(-56.22, -60) * mm, "construction": true});
            skLineSegment(sketch, "E120", {"start": v(-95, -70.01) * mm, "end": v(-95, -39.78) * mm, "construction": true});
            skLineSegment(sketch, "E121.bottom", {"start": v(-120, -50) * mm, "end": v(-70, -50) * mm});
            skLineSegment(sketch, "E121.top", {"start": v(-120, -70) * mm, "end": v(-70, -70) * mm});
            skLineSegment(sketch, "E121.left", {"start": v(-120, -50) * mm, "end": v(-120, -70) * mm});
            skLineSegment(sketch, "E121.right", {"start": v(-70, -50) * mm, "end": v(-70, -70) * mm});
            skSolve(sketch);
        }
        {
            var Q0;
            Q0=makeQuery(id+"F1.imprint","IMPRINT",FACE,{"disambiguationData":[TD([[makeQuery(id+"F1.imprint","IMPRINT",EDGE,{"derivedFrom":sQuery(id+"F1.wireOp",EDGE,"E58.bottom")}),-1.0]])]});
            var sketch = newSketch(context, id + "F2", { "sketchPlane" : qUnion([Q0])});
            skLineSegment(sketch, "E122.bottom", {"start": v(-145, -40) * mm, "end": v(-125, -40) * mm, "construction": true});
            skLineSegment(sketch, "E122.top", {"start": v(-145, -80) * mm, "end": v(-125, -80) * mm, "construction": true});
            skLineSegment(sketch, "E122.left", {"start": v(-145, -40) * mm, "end": v(-145, -80) * mm, "construction": true});
            skLineSegment(sketch, "E122.right", {"start": v(-125, -40) * mm, "end": v(-125, -80) * mm, "construction": true});
            skLineSegment(sketch, "E123", {"start": v(-125, -44) * mm, "end": v(-145, -44) * mm, "construction": true});
            skLineSegment(sketch, "E124", {"start": v(-125, -76) * mm, "end": v(-145, -76) * mm, "construction": true});
            skSolve(sketch);
        }
        {
            var Q0;
            Q0=makeQuery(id+"F1.imprint","IMPRINT",FACE,{"disambiguationData":[TD([[makeQuery(id+"F1.imprint","IMPRINT",EDGE,{"derivedFrom":sQuery(id+"F1.wireOp",EDGE,"E58.bottom")}),-1.0]])]});
            var sketch = newSketch(context, id + "F3", { "sketchPlane" : qUnion([Q0])});
            skLineSegment(sketch, "E125.bottom", {"start": v(-120, -43) * mm, "end": v(-45, -43) * mm, "construction": true});
            skLineSegment(sketch, "E125.top", {"start": v(-120, -83) * mm, "end": v(-45, -83) * mm, "construction": true});
            skLineSegment(sketch, "E125.left", {"start": v(-120, -43) * mm, "end": v(-120, -83) * mm, "construction": true});
            skLineSegment(sketch, "E125.right", {"start": v(-45, -43) * mm, "end": v(-45, -83) * mm, "construction": true});
            skLineSegment(sketch, "E126", {"start": v(-120, -78) * mm, "end": v(-45, -78) * mm, "construction": true});
            skCircle(sketch, "E127", {"center": v(-113, -78) * mm, "radius": 1.6 * mm});
            skCircle(sketch, "E128", {"center": v(-52, -78) * mm, "radius": 1.6 * mm});
            skSolve(sketch);
        }
        {
            var Q0;
            Q0=makeQuery(id+"F1.imprint","IMPRINT",FACE,{"disambiguationData":[TD([[makeQuery(id+"F1.imprint","IMPRINT",EDGE,{"derivedFrom":sQuery(id+"F1.wireOp",EDGE,"E58.bottom")}),-1.0]])]});
            var sketch = newSketch(context, id + "F4", { "sketchPlane" : qUnion([Q0])});
            skLineSegment(sketch, "E129.bottom", {"start": v(-110, 26) * mm, "end": v(-25, 26) * mm, "construction": true});
            skLineSegment(sketch, "E129.top", {"start": v(-110, -30) * mm, "end": v(-25, -30) * mm, "construction": true});
            skLineSegment(sketch, "E129.left", {"start": v(-110, 26) * mm, "end": v(-110, -30) * mm, "construction": true});
            skLineSegment(sketch, "E129.right", {"start": v(-25, 26) * mm, "end": v(-25, -30) * mm, "construction": true});
            skCircle(sketch, "E130", {"center": v(-84.5, -12) * mm, "radius": 1.5 * mm});
            skCircle(sketch, "E131", {"center": v(-30, 19.75) * mm, "radius": 1.5 * mm});
            skLineSegment(sketch, "E132.bottom", {"start": v(-10, 9) * mm, "end": v(0, 9) * mm});
            skLineSegment(sketch, "E132.top", {"start": v(-10, -9) * mm, "end": v(0, -9) * mm});
            skLineSegment(sketch, "E132.left", {"start": v(-10, 9) * mm, "end": v(-10, -9) * mm});
            skLineSegment(sketch, "E132.right", {"start": v(0, 9) * mm, "end": v(0, -9) * mm});
            skLineSegment(sketch, "E133", {"start": v(12.18, 0) * mm, "end": v(57.1, 0) * mm, "construction": true});
            skPoint(sketch, "E133.startSnap0", {"position": v(-10, 0) * mm});
            skLineSegment(sketch, "E134", {"start": v(-70, 26) * mm, "end": v(-70, -30) * mm, "construction": true});
            skSolve(sketch);
        }
        {
            var Q0;
            Q0=makeQuery(id+"F1.imprint","IMPRINT",FACE,{"disambiguationData":[TD([[makeQuery(id+"F1.imprint","IMPRINT",EDGE,{"derivedFrom":sQuery(id+"F1.wireOp",EDGE,"E58.bottom")}),-1.0]])]});
            var sketch = newSketch(context, id + "F5", { "sketchPlane" : qUnion([Q0])});
            skLineSegment(sketch, "E135.bottom", {"start": v(-85, 14) * mm, "end": v(-55, 14) * mm, "construction": true});
            skLineSegment(sketch, "E135.top", {"start": v(-85, -16) * mm, "end": v(-55, -16) * mm, "construction": true});
            skLineSegment(sketch, "E135.left", {"start": v(-85, 14) * mm, "end": v(-85, -16) * mm, "construction": true});
            skLineSegment(sketch, "E135.right", {"start": v(-55, 14) * mm, "end": v(-55, -16) * mm, "construction": true});
            skLineSegment(sketch, "E136.bottom", {"start": v(-82, 11) * mm, "end": v(-58, 11) * mm, "construction": true});
            skLineSegment(sketch, "E136.top", {"start": v(-82, -13) * mm, "end": v(-58, -13) * mm, "construction": true});
            skLineSegment(sketch, "E136.left", {"start": v(-82, 11) * mm, "end": v(-82, -13) * mm, "construction": true});
            skLineSegment(sketch, "E136.right", {"start": v(-58, 11) * mm, "end": v(-58, -13) * mm, "construction": true});
            skLineSegment(sketch, "E137.bottom", {"start": v(-90, 35) * mm, "end": v(-50, 35) * mm, "construction": true});
            skLineSegment(sketch, "E137.top", {"start": v(-90, -39) * mm, "end": v(-50, -39) * mm, "construction": true});
            skLineSegment(sketch, "E137.left", {"start": v(-90, 35) * mm, "end": v(-90, -39) * mm, "construction": true});
            skLineSegment(sketch, "E137.right", {"start": v(-50, 35) * mm, "end": v(-50, -39) * mm, "construction": true});
            skLineSegment(sketch, "E138", {"start": v(-90, 31) * mm, "end": v(-50, 31) * mm, "construction": true});
            skLineSegment(sketch, "E139", {"start": v(-90, -35) * mm, "end": v(-50, -35) * mm, "construction": true});
            skLineSegment(sketch, "E140", {"start": v(-85, 14) * mm, "end": v(-85, 35) * mm, "construction": true});
            skLineSegment(sketch, "E141", {"start": v(-58, 11) * mm, "end": v(-58, 31) * mm, "construction": true});
            skLineSegment(sketch, "E142", {"start": v(-58, -13) * mm, "end": v(-58, -35) * mm, "construction": true});
            skLineSegment(sketch, "E143", {"start": v(-82, -13) * mm, "end": v(-82, -35) * mm, "construction": true});
            skLineSegment(sketch, "E144", {"start": v(-82, 11) * mm, "end": v(-82, 31) * mm, "construction": true});
            skCircle(sketch, "E145", {"center": v(-82, 11) * mm, "radius": 1.6 * mm});
            skCircle(sketch, "E146", {"center": v(-58, 11) * mm, "radius": 1.6 * mm});
            skCircle(sketch, "E147", {"center": v(-58, 31) * mm, "radius": 1.6 * mm});
            skCircle(sketch, "E148", {"center": v(-82, 31) * mm, "radius": 1.6 * mm});
            skCircle(sketch, "E149", {"center": v(-58, -35) * mm, "radius": 1.6 * mm});
            skCircle(sketch, "E150", {"center": v(-82, -35) * mm, "radius": 1.6 * mm});
            skCircle(sketch, "E151", {"center": v(-58, -13) * mm, "radius": 1.6 * mm});
            skSolve(sketch);
        }
        {
            var Q0;
            Q0=makeQuery(id+"F1.imprint","IMPRINT",FACE,{"disambiguationData":[TD([[makeQuery(id+"F1.imprint","IMPRINT",EDGE,{"derivedFrom":sQuery(id+"F1.wireOp",EDGE,"E58.bottom")}),-1.0]])]});
            var sketch = newSketch(context, id + "F6", { "sketchPlane" : qUnion([Q0])});
            skLineSegment(sketch, "E152.bottom", {"start": v(-144, 85) * mm, "end": v(-34, 85) * mm, "construction": true});
            skLineSegment(sketch, "E152.top", {"start": v(-144, 63) * mm, "end": v(-34, 63) * mm, "construction": true});
            skLineSegment(sketch, "E152.left", {"start": v(-144, 85) * mm, "end": v(-144, 63) * mm, "construction": true});
            skLineSegment(sketch, "E152.right", {"start": v(-34, 85) * mm, "end": v(-34, 63) * mm, "construction": true});
            skSolve(sketch);
        }
        {
            var Q0;
            Q0=makeQuery(id+"F1.imprint","IMPRINT",FACE,{"disambiguationData":[TD([[makeQuery(id+"F1.imprint","IMPRINT",EDGE,{"derivedFrom":sQuery(id+"F1.wireOp",EDGE,"E58.bottom")}),-1.0]])]});
            var sketch = newSketch(context, id + "F7", { "sketchPlane" : qUnion([Q0])});
            skLineSegment(sketch, "E153", {"start": v(-39, 70) * mm, "end": v(-65.08, 70) * mm, "construction": true});
            skLineSegment(sketch, "E154", {"start": v(-60, 73.26) * mm, "end": v(-60, 65.24) * mm, "construction": true});
            skLineSegment(sketch, "E155", {"start": v(-25, 72.17) * mm, "end": v(-25, 61.98) * mm, "construction": true});
            skCircle(sketch, "E156", {"center": v(-60, 70) * mm, "radius": 1.6 * mm});
            skCircle(sketch, "E157", {"center": v(-25, 70.02) * mm, "radius": 1.6 * mm});
            skSolve(sketch);
        }
        {
            var Q0;
            Q0=makeQuery(id+"F1.imprint","IMPRINT",FACE,{"disambiguationData":[TD([[makeQuery(id+"F1.imprint","IMPRINT",EDGE,{"derivedFrom":sQuery(id+"F1.wireOp",EDGE,"E58.bottom")}),-1.0]])]});
            var sketch = newSketch(context, id + "F8", { "sketchPlane" : qUnion([Q0])});
            skLineSegment(sketch, "E158", {"start": v(10, 80) * mm, "end": v(10, 27.2) * mm, "construction": true});
            skCircle(sketch, "E159", {"center": v(10, 80) * mm, "radius": 1.6 * mm});
            skCircle(sketch, "E160", {"center": v(10, 27.2) * mm, "radius": 1.6 * mm});
            skLineSegment(sketch, "E161", {"start": v(20, 80) * mm, "end": v(20, 27.2) * mm, "construction": true});
            skCircle(sketch, "E162", {"center": v(20, 80) * mm, "radius": 1.6 * mm});
            skCircle(sketch, "E163", {"center": v(20, 27.2) * mm, "radius": 1.6 * mm});
            skLineSegment(sketch, "E164", {"start": v(10, 27.2) * mm, "end": v(0, 27.2) * mm, "construction": true});
            skCircle(sketch, "E165", {"center": v(0, 27.2) * mm, "radius": 1.6 * mm});
            skSolve(sketch);
        }
        {
            var Q0;
            Q0=makeQuery(id+"F1.imprint","IMPRINT",FACE,{"disambiguationData":[TD([[makeQuery(id+"F1.imprint","IMPRINT",EDGE,{"derivedFrom":sQuery(id+"F1.wireOp",EDGE,"E58.bottom")}),-1.0]])]});
            var sketch = newSketch(context, id + "F9", { "sketchPlane" : qUnion([Q0])});
            skLineSegment(sketch, "E166", {"start": v(15, -75) * mm, "end": v(70.88, -75) * mm, "construction": true});
            skCircle(sketch, "E167", {"center": v(15, -75) * mm, "radius": 1.6 * mm});
            skCircle(sketch, "E168", {"center": v(70.88, -75) * mm, "radius": 1.6 * mm});
            skCircle(sketch, "E169", {"center": v(60.88, -75) * mm, "radius": 1.6 * mm});
            skCircle(sketch, "E170", {"center": v(50.88, -75) * mm, "radius": 1.6 * mm});
            skSolve(sketch);
        }
        {
            var Q0;
            Q0 = qSketchRegion(id + "F1", true);
            extrude(context, id + "F10", {"entities" : qUnion([Q0]), "depth" : 5 * mm});
        }
        {
            var Q0;
            Q0 = qSketchRegion(id + "F2", true);
            var Q1;
            Q1 = qSketchRegion(id + "F3", true);
            var Q2;
            Q2 = qSketchRegion(id + "F4", true);
            var Q3;
            Q3 = qSketchRegion(id + "F5", true);
            var Q4;
            Q4 = qSketchRegion(id + "F6", true);
            var Q5;
            Q5 = qSketchRegion(id + "F7", true);
            var Q6;
            Q6 = qSketchRegion(id + "F8", true);
            var Q7;
            Q7 = qSketchRegion(id + "F9", true);
            extrude(context, id + "F11", {"entities" : qUnion([Q0, Q1, Q2, Q3, Q4, Q5, Q6, Q7]), "operationType" : NewBodyOperationType.REMOVE, "depth" : 5 * mm});
        }
    });
